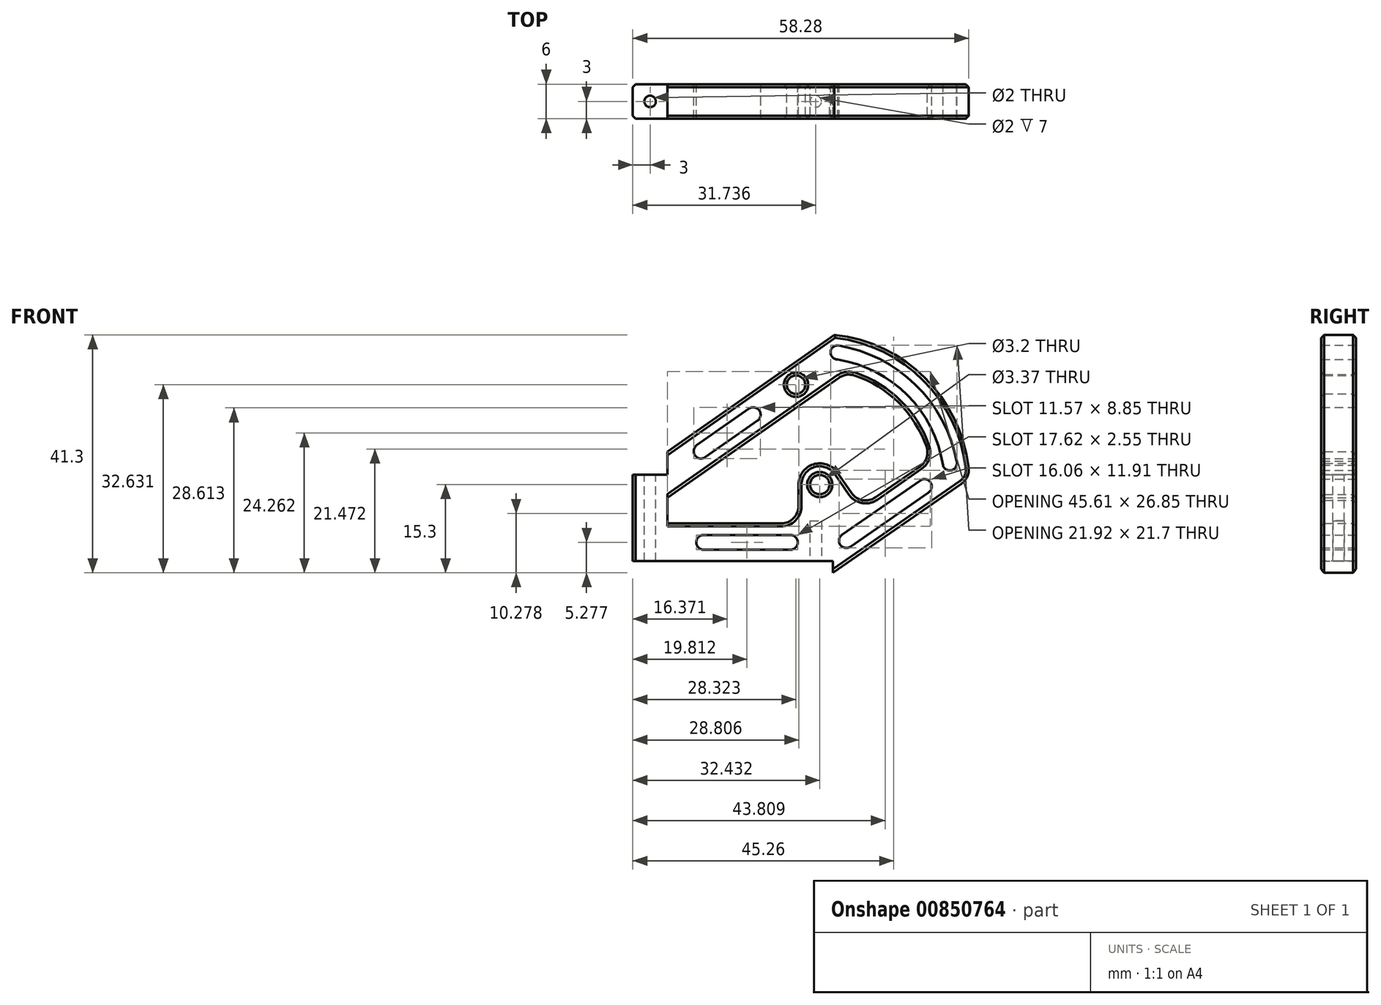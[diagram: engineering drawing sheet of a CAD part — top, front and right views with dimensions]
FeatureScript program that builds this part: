
annotation { "Feature Type Name" : "Feature", "Feature Type Description" : "" }
export const myFeature = defineFeature(function(context is Context, id is Id, definition is map)
    precondition{}
    {
        {
            var Q0;
            Q0=qCreatedBy(makeId("Top.planeOp"),FACE);
            var sketch = newSketch(context, id + "F0", { "sketchPlane" : qUnion([Q0])});
            skLineSegment(sketch, "E0", {"start": v(0, 0) * mm, "end": v(31, 0) * mm, "construction": true});
            skLineSegment(sketch, "E1", {"start": v(31, 0) * mm, "end": v(31, 20) * mm, "construction": true});
            skLineSegment(sketch, "E2", {"start": v(31, 0) * mm, "end": v(31, -20) * mm, "construction": true});
            skCircle(sketch, "E3", {"center": v(28, 17) * mm, "radius": 1 * mm});
            skLineSegment(sketch, "E4", {"start": v(28, 17) * mm, "end": v(31, 17) * mm, "construction": true});
            skLineSegment(sketch, "E5", {"start": v(31, 17) * mm, "end": v(31, 20) * mm, "construction": true});
            skLineSegment(sketch, "E6.bottom", {"start": v(31, 20) * mm, "end": v(25, 20) * mm});
            skLineSegment(sketch, "E6.top", {"start": v(31, 14) * mm, "end": v(25, 14) * mm});
            skLineSegment(sketch, "E6.left", {"start": v(31, 20) * mm, "end": v(31, 14) * mm});
            skLineSegment(sketch, "E6.right", {"start": v(25, 20) * mm, "end": v(25, 14) * mm});
            skLineSegment(sketch, "E7.MirrorCS", {"start": v(0, 0) * mm, "end": v(-31, 0) * mm, "construction": true});
            skLineSegment(sketch, "E8", {"start": v(-31, 0) * mm, "end": v(-31, 17) * mm, "construction": true});
            skSolve(sketch);
        }
        {
            var Q0;
            Q0 = qSketchRegion(id + "F0", true);
            var Q1;
            Q1=makeQuery(id+"F0.imprint","IMPRINT",FACE,{"disambiguationData":[TD([[makeQuery(id+"F0.imprint","IMPRINT",EDGE,{"derivedFrom":sQuery(id+"F0.wireOp",EDGE,"E3")}),1.0]])]});
            extrude(context, id + "F1", {"entities" : qUnion([Q0, Q1]), "oppositeDirection" : true, "depth" : 15 * mm, "offsetDistance" : 25 * mm});
        }
        {
            var Q0;
            Q0=makeQuery(id+"F0.imprint","IMPRINT",FACE,{"disambiguationData":[TD([[makeQuery(id+"F0.imprint","IMPRINT",EDGE,{"derivedFrom":sQuery(id+"F0.wireOp",EDGE,"E3")}),1.0]])]});
            extrude(context, id + "F2", {"entities" : qUnion([Q0]), "operationType" : NewBodyOperationType.REMOVE, "endBound" : BoundingType.UP_TO_NEXT, "oppositeDirection" : true, "depth" : 5 * mm, "offsetDistance" : 25 * mm});
        }
        {
            var Q0;
            Q0=makeQuery(id+"F1.opExtrude","SWEPT_FACE",FACE,{"disambiguationData":[OSD([sQuery(id+"F0.wireOp",EDGE,"E6.bottom")])]});
            var sketch = newSketch(context, id + "F3", { "sketchPlane" : qUnion([Q0])});
            skLineSegment(sketch, "E9", {"start": v(-31, 0) * mm, "end": v(-31, 4) * mm});
            skLineSegment(sketch, "E10", {"start": v(-31, 4) * mm, "end": v(-39.77, 4) * mm, "construction": true});
            skLineSegment(sketch, "E11", {"start": v(-31, 4) * mm, "end": v(-59.99, 24.3) * mm});
            skLineSegment(sketch, "E12", {"start": v(-59.74, -15) * mm, "end": v(-31, -15) * mm});
            skLineSegment(sketch, "E13", {"start": v(-31, 0) * mm, "end": v(-31, -4) * mm, "construction": true});
            skLineSegment(sketch, "E14", {"start": v(-31, -4) * mm, "end": v(-61.96, 17.68) * mm});
            skLineSegment(sketch, "E15", {"start": v(-53.75, -8.45) * mm, "end": v(-31, -8.45) * mm});
            skLineSegment(sketch, "E16", {"start": v(-31, -8.45) * mm, "end": v(-31, -4) * mm});
            skPoint(sketch, "E17.orphan", {"position": v(-31, -15) * mm});
            skLineSegment(sketch, "E18", {"start": v(-55.2, 12.95) * mm, "end": v(-51.44, 18.31) * mm, "construction": true});
            skCircle(sketch, "E19", {"center": v(-53.32, 15.63) * mm, "radius": 1.6 * mm});
            skLineSegment(sketch, "E20", {"start": v(-44.81, -15) * mm, "end": v(-44.81, -8.45) * mm, "construction": true});
            skLineSegment(sketch, "E21", {"start": v(-44.81, -11.72) * mm, "end": v(-48.42, -11.72) * mm, "construction": true});
            skLineSegment(sketch, "E22", {"start": v(-48.42, -11.72) * mm, "end": v(-37.28, -11.72) * mm, "construction": true});
            skLineSegment(sketch, "E23.bottom", {"start": v(-37.28, -10.45) * mm, "end": v(-52.34, -10.45) * mm});
            skLineSegment(sketch, "E23.top", {"start": v(-37.28, -13) * mm, "end": v(-52.34, -13) * mm});
            skLineSegment(sketch, "E23.left", {"start": v(-37.28, -10.45) * mm, "end": v(-37.28, -13) * mm, "construction": true});
            skLineSegment(sketch, "E23.right", {"start": v(-52.34, -10.45) * mm, "end": v(-52.34, -13) * mm, "construction": true});
            skPoint(sketch, "E23.middle", {"position": v(-44.81, -11.72) * mm});
            skArc(sketch, "E24", {"start": v(-52.34, -10.45) * mm, "mid": v(-53.62, -11.72) * mm, "end": v(-52.34, -13) * mm});
            skArc(sketch, "E25", {"start": v(-37.28, -13) * mm, "mid": v(-36, -11.72) * mm, "end": v(-37.28, -10.45) * mm});
            skLineSegment(sketch, "E26", {"start": v(-76.3, -3.07) * mm, "end": v(-62.76, -12.47) * mm});
            skLineSegment(sketch, "E27", {"start": v(-53.32, 15.63) * mm, "end": v(-46.94, 11.16) * mm});
            skArc(sketch, "E28", {"start": v(-37.58, 3.05) * mm, "mid": v(-35.8, 3.36) * mm, "end": v(-36.11, 5.14) * mm});
            skArc(sketch, "E29", {"start": v(-45.17, 11.48) * mm, "mid": v(-46.94, 11.16) * mm, "end": v(-46.63, 9.39) * mm});
            skLineSegment(sketch, "E30", {"start": v(-45.17, 11.48) * mm, "end": v(-44.02, 13.12) * mm, "construction": true});
            skLineSegment(sketch, "E31", {"start": v(-44.02, 13.12) * mm, "end": v(-46.63, 9.39) * mm, "construction": true});
            skLineSegment(sketch, "E32", {"start": v(-46.63, 9.39) * mm, "end": v(-37.58, 3.05) * mm});
            skLineSegment(sketch, "E33", {"start": v(-37.58, 3.05) * mm, "end": v(-36.11, 5.14) * mm, "construction": true});
            skLineSegment(sketch, "E34", {"start": v(-36.11, 5.14) * mm, "end": v(-45.17, 11.48) * mm});
            skLineSegment(sketch, "E35.trimOffspring", {"start": v(-45.9, 10.43) * mm, "end": v(-36.84, 4.1) * mm});
            skLineSegment(sketch, "E36", {"start": v(-53.32, 15.63) * mm, "end": v(-61.86, 21.61) * mm, "construction": true});
            skLineSegment(sketch, "E37", {"start": v(-61.86, 21.61) * mm, "end": v(-59.99, 24.3) * mm, "construction": true});
            skLineSegment(sketch, "E38", {"start": v(-53.32, 15.63) * mm, "end": v(-32.88, 1.32) * mm, "construction": true});
            skLineSegment(sketch, "E39", {"start": v(-32.88, 1.32) * mm, "end": v(-31, 4) * mm, "construction": true});
            skLineSegment(sketch, "E40", {"start": v(-62.62, -15) * mm, "end": v(-83.41, -0.58) * mm});
            skLineSegment(sketch, "E41", {"start": v(-64.64, -5.63) * mm, "end": v(-76.57, 2.65) * mm});
            skArc(sketch, "E42.trimOffspring", {"start": v(-59.99, 24.3) * mm, "mid": v(-76.3, 16.18) * mm, "end": v(-83.41, -0.58) * mm});
            skArc(sketch, "E43.trimOffspring", {"start": v(-61.96, 17.68) * mm, "mid": v(-71.4, 12.23) * mm, "end": v(-76.57, 2.65) * mm});
            skLineSegment(sketch, "E44.trimOffspring", {"start": v(-78.8, 1.65) * mm, "end": v(-81.18, 2.35) * mm, "construction": true});
            skArc(sketch, "E45", {"start": v(-81.18, 2.35) * mm, "mid": v(-80.34, 0.8) * mm, "end": v(-78.8, 1.65) * mm});
            skLineSegment(sketch, "E46.trimOffspring", {"start": v(-60.5, 20.01) * mm, "end": v(-60.55, 22.46) * mm, "construction": true});
            skArc(sketch, "E47", {"start": v(-60.5, 20.01) * mm, "mid": v(-59.3, 21.26) * mm, "end": v(-60.55, 22.46) * mm});
            skArc(sketch, "E48.trimOffspring", {"start": v(-60.5, 20.01) * mm, "mid": v(-72.65, 13.81) * mm, "end": v(-78.8, 1.65) * mm});
            skArc(sketch, "E49.trimOffspring", {"start": v(-60.55, 22.46) * mm, "mid": v(-74.02, 15.65) * mm, "end": v(-81.18, 2.35) * mm});
            skLineSegment(sketch, "E50", {"start": v(-61.3, -10.37) * mm, "end": v(-74.85, -0.98) * mm});
            skLineSegment(sketch, "E51", {"start": v(-62.04, -11.42) * mm, "end": v(-62.76, -12.47) * mm});
            skArc(sketch, "E52", {"start": v(-62.76, -12.47) * mm, "mid": v(-60.99, -12.15) * mm, "end": v(-61.3, -10.37) * mm});
            skLineSegment(sketch, "E53", {"start": v(-74.85, -0.98) * mm, "end": v(-75.58, -2.03) * mm});
            skArc(sketch, "E54", {"start": v(-74.85, -0.98) * mm, "mid": v(-76.63, -1.3) * mm, "end": v(-76.3, -3.07) * mm});
            skLineSegment(sketch, "E55", {"start": v(-45.17, 11.48) * mm, "end": v(-64.85, 25.26) * mm, "construction": true});
            skLineSegment(sketch, "E56", {"start": v(-74.85, -0.98) * mm, "end": v(-84.58, 5.77) * mm, "construction": true});
            skLineSegment(sketch, "E57", {"start": v(-52.34, -10.45) * mm, "end": v(-65.1, -10.45) * mm, "construction": true});
            skCircle(sketch, "E58", {"center": v(-57.43, -1.7) * mm, "radius": 1.69 * mm});
            skLineSegment(sketch, "E59", {"start": v(-62.62, -15) * mm, "end": v(-59.74, -17) * mm});
            skLineSegment(sketch, "E60", {"start": v(-59.74, -17) * mm, "end": v(-59.74, -15) * mm});
            skCircle(sketch, "E61", {"center": v(-57.43, -1.7) * mm, "radius": 3.69 * mm});
            skLineSegment(sketch, "E62", {"start": v(-53.75, -8.45) * mm, "end": v(-53.75, -1.7) * mm});
            skLineSegment(sketch, "E63", {"start": v(-64.64, -5.63) * mm, "end": v(-60.45, 0.41) * mm});
            skLineSegment(sketch, "E64", {"start": v(-78.8, 1.65) * mm, "end": v(-60.5, 20.01) * mm, "construction": true});
            skPoint(sketch, "E65.start.orphan", {"position": v(-69.65, 10.83) * mm});
            skSolve(sketch);
        }
        {
            var Q0;
            {var subQ3=sQuery(id+"F3.wireOp",EDGE,"E9");Q0=makeQuery(id+"F3.imprint","IMPRINT",FACE,{"disambiguationData":[TD([[makeQuery(id+"F3.imprint","IMPRINT",EDGE,{"derivedFrom":subQ3}),1.0]])]});}
            var Q1;
            {var subQ0=sQuery(id+"F3.wireOp",EDGE,"aZAlumgZ-XeYx-SgPZ-gMWN-ny0Q0VMRnAjb");Q1=makeQuery(id+"F3.imprint","IMPRINT",FACE,{"disambiguationData":[TD([[makeQuery(id+"F3.imprint","IMPRINT",EDGE,{"derivedFrom":subQ0}),-1.0]])]});}
            var Q2;
            Q2=makeQuery(id+"F3.imprint","IMPRINT",FACE,{"disambiguationData":[TD([[makeQuery(id+"F3.imprint","IMPRINT",EDGE,{"derivedFrom":sQuery(id+"F3.wireOp",EDGE,"DYYVoYpd-ECQO-Ccpg-T7KX-dFPmmB7n3uXs")}),-1.0]])]});
            var Q3;
            Q3=makeQuery(id+"F3.imprint","IMPRINT",FACE,{"disambiguationData":[TD([[makeQuery(id+"F3.imprint","IMPRINT",EDGE,{"derivedFrom":sQuery(id+"F3.wireOp",EDGE,"E58")}),-1.0]])]});
            extrude(context, id + "F4", {"entities" : qUnion([Q0, Q1, Q2, Q3]), "oppositeDirection" : true, "depth" : 6 * mm, "offsetDistance" : 25 * mm});
        }
        {
            var Q0;
            Q0=makeQuery(id+"F4.opExtrude","SWEPT_BODY",BODY,{"disambiguationData":[OSD([sQuery(id+"F0.wireOp",EDGE,"E6.bottom"),sQuery(id+"F0.wireOp",EDGE,"E6.left"),sQuery(id+"F3.wireOp",EDGE,"E9"),sQuery(id+"F3.wireOp",EDGE,"E11"),sQuery(id+"F3.wireOp",EDGE,"7eqV1mgg-43Ij-rjHs-3Qu8-d29UOZqboB1S"),sQuery(id+"F3.wireOp",EDGE,"SY7YKMZi-hSA7-JE9x-1azf-V4d5JSeuqVt1"),sQuery(id+"F3.wireOp",EDGE,"E12"),sQuery(id+"F3.wireOp",EDGE,"E14"),sQuery(id+"F3.wireOp",EDGE,"0Tv07qa9-Fb4J-FoAp-sbSr-NNi5uEDryg0i"),sQuery(id+"F3.wireOp",EDGE,"xWPwM4UM-FEz1-k5V9-iMb6-zDkujl0GUq6u"),sQuery(id+"F3.wireOp",EDGE,"E15")])]});
            var Q1;
            Q1=makeQuery(id+"F1.opExtrude","SWEPT_BODY",BODY,{"disambiguationData":[OSD([sQuery(id+"F0.wireOp",EDGE,"E6.bottom"),sQuery(id+"F0.wireOp",EDGE,"E6.top"),sQuery(id+"F0.wireOp",EDGE,"E6.left"),sQuery(id+"F0.wireOp",EDGE,"E6.right")])]});
            booleanBodies(context, id + "F5", {"operationType" : BooleanOperationType.UNION, "tools" : qUnion([Q0, Q1])});
        }
        {
            var Q0;
            Q0=makeQuery(id+"F4.opExtrude","SWEPT_EDGE",EDGE,{"disambiguationData":[OSD([sQuery(id+"F3.wireOp",EDGE,"E41"),sQuery(id+"F3.wireOp",EDGE,"CydtGTrg-XAyj-ZKm5-L5w0-0841wxQPktTv")])]});
            var Q1;
            Q1=makeQuery(id+"F4.opExtrude","SWEPT_EDGE",EDGE,{"disambiguationData":[OSD([sQuery(id+"F3.wireOp",EDGE,"E15"),sQuery(id+"F3.wireOp",EDGE,"G3v5Q8E4-bjQw-wBDf-Wb4y-pMVCfv20Idvw")])]});
            var Q2;
            Q2=makeQuery(id+"F4.opExtrude","SWEPT_EDGE",EDGE,{"disambiguationData":[OSD([sQuery(id+"F3.wireOp",EDGE,"E41"),sQuery(id+"F3.wireOp",EDGE,"E43.trimOffspring")])]});
            var Q3;
            Q3=makeQuery(id+"F4.opExtrude","SWEPT_EDGE",EDGE,{"disambiguationData":[OSD([sQuery(id+"F3.wireOp",EDGE,"E14"),sQuery(id+"F3.wireOp",EDGE,"E43.trimOffspring")])]});
            var Q4;
            Q4=makeQuery(id+"F4.opExtrude","SWEPT_EDGE",EDGE,{"disambiguationData":[OSD([sQuery(id+"F0.wireOp",EDGE,"E6.bottom"),sQuery(id+"F0.wireOp",EDGE,"E6.left"),sQuery(id+"F3.wireOp",EDGE,"E15"),sQuery(id+"F3.wireOp",EDGE,"E16")])]});
            var Q5;
            Q5=makeQuery(id+"F4.opExtrude","SWEPT_EDGE",EDGE,{"disambiguationData":[OSD([sQuery(id+"F0.wireOp",EDGE,"E6.bottom"),sQuery(id+"F0.wireOp",EDGE,"E6.left"),sQuery(id+"F3.wireOp",EDGE,"E14"),sQuery(id+"F3.wireOp",EDGE,"E16")])]});
            var Q6;
            Q6=makeQuery(id+"F4.opExtrude","SWEPT_EDGE",EDGE,{"disambiguationData":[OSD([sQuery(id+"F3.wireOp",EDGE,"E40"),sQuery(id+"F3.wireOp",EDGE,"E42.trimOffspring")])]});
            fillet(context, id + "F6", {"entities" : qUnion([Q0, Q1, Q2, Q3, Q4, Q5, Q6]), "radius" : 3 * mm, "tangentPropagation" : true, "allowEdgeOverflow" : false});
        }
        {
            var Q0;
            Q0=makeQuery(id+"F5.opBoolean","MERGE",FACE,{"derivedFrom":[makeQuery(id+"F1.opExtrude","CAP_FACE",FACE,{"disambiguationData":[OSD([sQuery(id+"F0.wireOp",EDGE,"E6.bottom"),sQuery(id+"F0.wireOp",EDGE,"E6.top"),sQuery(id+"F0.wireOp",EDGE,"E6.left"),sQuery(id+"F0.wireOp",EDGE,"E6.right")])],"isStart":false}),makeQuery(id+"F4.opExtrude","SWEPT_FACE",FACE,{"disambiguationData":[OSD([sQuery(id+"F3.wireOp",EDGE,"E12")])]})]});
            var sketch = newSketch(context, id + "F7", { "sketchPlane" : qUnion([Q0])});
            skCircle(sketch, "E66", {"center": v(56.74, -17) * mm, "radius": 1 * mm});
            skSolve(sketch);
        }
        {
            var Q0;
            Q0 = qSketchRegion(id + "F7", true);
            extrude(context, id + "F8", {"entities" : qUnion([Q0]), "operationType" : NewBodyOperationType.REMOVE, "oppositeDirection" : true, "depth" : 7 * mm, "offsetDistance" : 25 * mm});
        }
        {
            var Q0;
            Q0=makeQuery(id+"F4.opExtrude","CAP_EDGE",EDGE,{"disambiguationData":[OSD([sQuery(id+"F3.wireOp",EDGE,"E42.trimOffspring")])],"isStart":true});
            var Q1;
            Q1=makeQuery(id+"F4.opExtrude","CAP_EDGE",EDGE,{"disambiguationData":[OSD([sQuery(id+"F3.wireOp",EDGE,"E58")])],"isStart":true});
            var Q2;
            Q2=makeQuery(id+"F4.opExtrude","CAP_EDGE",EDGE,{"disambiguationData":[OSD([sQuery(id+"F3.wireOp",EDGE,"E41")])],"isStart":true});
            var Q3;
            Q3=makeQuery(id+"F4.opExtrude","CAP_EDGE",EDGE,{"disambiguationData":[OSD([sQuery(id+"F3.wireOp",EDGE,"E61")])],"isStart":true});
            var Q4;
            Q4=makeQuery(id+"F4.opExtrude","CAP_EDGE",EDGE,{"disambiguationData":[OSD([sQuery(id+"F3.wireOp",EDGE,"E40"),sQuery(id+"F3.wireOp",EDGE,"E59")])],"isStart":false});
            var Q5;
            Q5=makeQuery(id+"F4.opExtrude","CAP_EDGE",EDGE,{"disambiguationData":[OSD([sQuery(id+"F3.wireOp",EDGE,"E11")])],"isStart":false});
            var Q6;
            Q6=makeQuery(id+"F4.opExtrude","CAP_EDGE",EDGE,{"disambiguationData":[OSD([sQuery(id+"F3.wireOp",EDGE,"E15")])],"isStart":false});
            var Q7;
            Q7=makeQuery(id+"F4.opExtrude","CAP_EDGE",EDGE,{"disambiguationData":[OSD([sQuery(id+"F3.wireOp",EDGE,"E58")])],"isStart":false});
            var Q8;
            Q8=makeQuery(id+"F4.opExtrude","CAP_EDGE",EDGE,{"disambiguationData":[OSD([sQuery(id+"F3.wireOp",EDGE,"E41")])],"isStart":false});
            var Q9;
            Q9=makeQuery(id+"F4.opExtrude","CAP_EDGE",EDGE,{"disambiguationData":[OSD([sQuery(id+"F3.wireOp",EDGE,"E11")])],"isStart":true});
            var Q10;
            Q10=makeQuery(id+"F1.opExtrude","SWEPT_EDGE",EDGE,{"disambiguationData":[OSD([sQuery(id+"F0.wireOp",EDGE,"E6.bottom"),sQuery(id+"F0.wireOp",EDGE,"E6.right")])]});
            var Q11;
            Q11=makeQuery(id+"F1.opExtrude","SWEPT_EDGE",EDGE,{"disambiguationData":[OSD([sQuery(id+"F0.wireOp",EDGE,"E6.top"),sQuery(id+"F0.wireOp",EDGE,"E6.right")])]});
            var Q12;
            Q12=makeQuery(id+"F4.opExtrude","CAP_EDGE",EDGE,{"disambiguationData":[OSD([sQuery(id+"F3.wireOp",EDGE,"E19")])],"isStart":true});
            var Q13;
            Q13=makeQuery(id+"F4.opExtrude","CAP_EDGE",EDGE,{"disambiguationData":[OSD([sQuery(id+"F3.wireOp",EDGE,"E19")])],"isStart":false});
            chamfer(context, id + "F9", {"entities" : qUnion([Q0, Q1, Q2, Q3, Q4, Q5, Q6, Q7, Q8, Q9, Q10, Q11, Q12, Q13]), "width" : 0.5 * mm, "tangentPropagation" : true});
        }
    });
